# Revit family: Legrand-Ups-Keor_HPE-60_500kVA
name_source: partatom
category: Apparecchi elettrici
revit_build: Autodesk Revit 2018 (Build: 20170927_1515(x64)
units: mm (PartAtom-declared; Revit-internal decimal feet)

## family parameters
Basato su piano di lavoro = No
Condiviso = No
Mantenere orientamento annotazione = No
Numero OmniClass = 23.80.10.17.34
Punto di calcolo locali = No
Quota connettore circolare = Usa diametro
Sempre verticale = Sì
Taglio con vuoti quando caricato = No
Tipo di parte = Normale
Titolo OmniClass = Static Uninterruptible Power Supplies

## types (13) — shared parameters
Back Clearance = 50 mm  [stored 0.164042 ft]
Conductors = Cables
Connection constraint = Ahead and bottom
Connection constraint (signal) = Ahead and above/bottom
Frequency of use = 50 Hz or 60 Hz selectable
Front Clearance = 1200 mm
Humidity = 0-95% not condensing
Input / Output phase configuration = 3ph+N+PE/3ph+N+PE
Installation type = On the floor
Modello = KEOR HP
Operating altitude = up to 1000 m altitude without derating
Operating temperature = from 0°C to +40°C
Output Voltage = 380,400,415 Vac
Output power factor = 1
Produttore = LEGRAND
Top clearance = 600 mm
URL = https://ups.legrand.com
Visibilità aree d'installazione = Sì

## per-type parameters (varying)
| type | Active power of use | Battery number (9Ah) | Cabinet Depth | Cabinet Height | Cabinet Width | Installation space | Max sound pressure level | Nominal Power | Side Clearance | Weight |
| LG-311087 | 60 kW | 0 | 940 mm | 1500 mm  [stored 4.92126 ft] | 560 mm  [stored 1.83727 ft] | 0.52 m³ | < 60 dB at 1m | 60 kVA | 600 mm | 225.0 kg |
| LG-960569 | 100 kW | 0 | 940 mm | 1800 mm  [stored 5.90551 ft] | 560 mm  [stored 1.83727 ft] | 0.52 m³ | < 60 dB at 1m | 100 kVA | 600 mm | 320.0 kg |
| LG-311088 | 60 kW | 120 | 940 mm | 1500 mm  [stored 4.92126 ft] | 560 mm  [stored 1.83727 ft] | 0.52 m³ | < 60 dB at 1m | 60 kVA | 600 mm | 525.0 kg |
| LG-311089 | 60 kW | 180 | 940 mm | 1500 mm  [stored 4.92126 ft] | 560 mm  [stored 1.83727 ft] | 0.52 m³ | < 60 dB at 1m | 60 kVA | 600 mm | 675.0 kg |
| LG-311090 | 80 kW | 0 | 940 mm | 1500 mm  [stored 4.92126 ft] | 560 mm  [stored 1.83727 ft] | 0.52 m³ | < 60 dB at 1m | 80 kVA | 600 mm | 250.0 kg |
| LG-311091 | 80 kW | 180 | 940 mm | 1500 mm  [stored 4.92126 ft] | 560 mm  [stored 1.83727 ft] | 0.52 m³ | < 60 dB at 1m | 80 kVA | 600 mm | 700.0 kg |
| LG-953502 | 400 kW | 0 | 970 mm  [stored 3.18241 ft] | 1978 mm  [stored 6.4895 ft] | 1430 mm  [stored 4.6916 ft] | 1.38 m³ | < 72 dB at 1m | 400 kVA | 50 mm  [stored 0.164042 ft] | 1080.0 kg |
| LG-953503 | 500 kW | 0 | 970 mm  [stored 3.18241 ft] | 1978 mm  [stored 6.4895 ft] | 1430 mm  [stored 4.6916 ft] | 1.38 m³ | < 72 dB at 1m | 500 kVA | 50 mm  [stored 0.164042 ft] | 1250.0 kg |
| LG-960570 | 125 kW | 0 | 940 mm | 1800 mm  [stored 5.90551 ft] | 560 mm  [stored 1.83727 ft] | 0.52 m³ | < 60 dB at 1m | 125 kVA | 600 mm | 360.0 kg |
| LG-960571 | 160 kW | 0 | 940 mm | 1800 mm  [stored 5.90551 ft] | 560 mm  [stored 1.83727 ft] | 0.52 m³ | < 60 dB at 1m | 160 kVA | 600 mm | 380.0 kg |
| LG-960572 | 200 kW | 0 | 940 mm | 1800 mm  [stored 5.90551 ft] | 560 mm  [stored 1.83727 ft] | 0.52 m³ | < 65 dB at 1m | 200 kVA | 600 mm | 720.0 kg |
| LG-953500 | 250 kW | 0 | 966 mm | 1975 mm  [stored 6.47966 ft] | 850 mm  [stored 2.78871 ft] | 0.82 m³ | < 65 dB at 1m | 250 kVA | 600 mm | 850.0 kg |
| LG-953501 | 300 kW | 0 | 966 mm | 1975 mm  [stored 6.47966 ft] | 850 mm  [stored 2.78871 ft] | 0.52 m³ | < 65 dB at 1m | 300 kVA | 600 mm | 900.0 kg |

note: [stored X ft] marks values corroborated as IEEE doubles in the binary element streams (Revit-internal decimal feet)
